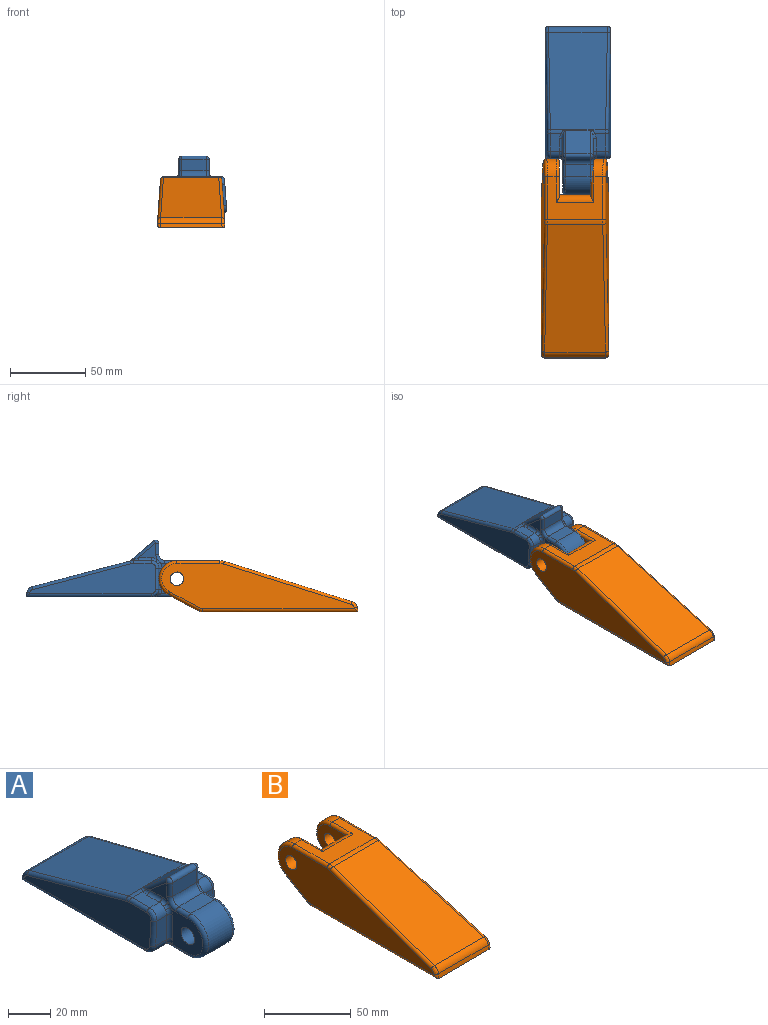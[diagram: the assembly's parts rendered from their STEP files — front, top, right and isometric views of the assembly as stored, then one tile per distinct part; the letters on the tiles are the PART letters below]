
ASSEMBLY  parts=2 mates=1
PART A: 80 faces, bbox 43.7x113x38.7 mm
  f0: plane 21.21x20.93mm, normal (1,0,0), area 295.5mm2, adj f21,f47,f48,f49,f58,f60,f61,f62
  f1: plane 21.21x20.93mm, normal (-1,0,0), area 295.5mm2, adj f21,f44,f45,f46,f54,f76,f77,f78
  f2: plane 11.71x6.91mm, normal (0,0,1), area 74.4mm2, adj f3,f10,f36,f65,f66
  f3: cylinder r=5mm len=6.51mm, axis (-1,0,0), area 50.3mm2, adj f2,f4,f35,f62,f63,f64
  f4: plane 14x7.48mm, normal (0,-1,0), area 97.9mm2, adj f3,f5,f37,f61
  f5: cylinder r=5mm len=11.69mm, axis (-1,0,0), area 68.1mm2, adj f4,f6,f39,f59,f60
  f6: plane 100x39.39mm, normal (0,0,-1), area 3541.3mm2, adj f5,f7,f14,f20,f32,f41,f44,f47
  f7: plane 39.72x2.75mm, normal (0,0.98,0.17), area 110.5mm2, adj f6,f8,f32,f34,f41,f43
  f8: cylinder r=5mm len=39.33mm, axis (-1,0,0), area 223.2mm2, adj f7,f9,f33,f42
  f9: plane 64.62x39.01mm, normal (0,0.25,0.97), area 2517.9mm2, adj f8,f10,f15,f31,f40,f68,f69,f70
  f10: cylinder r=10mm len=9.08mm, axis (-1,0,0), area 20mm2, adj f2,f9,f38,f67
  f11: plane 11.71x6.91mm, normal (0,0,1), area 74.4mm2, adj f12,f15,f27,f72,f73
  f12: cylinder r=5mm len=6.51mm, axis (-1,0,0), area 50.3mm2, adj f11,f13,f26,f74,f75,f76
  f13: plane 14x7.48mm, normal (0,-1,0), area 97.9mm2, adj f12,f14,f28,f77
  f14: cylinder r=5mm len=11.69mm, axis (-1,0,0), area 68.1mm2, adj f6,f13,f30,f78,f79
  f15: cylinder r=10mm len=9.08mm, axis (-1,0,0), area 20mm2, adj f9,f11,f29,f71
  f16: plane 16x15.61mm, normal (0,0.65,0.76), area 327.5mm2, adj f17,f51,f55,f69
  f17: cylinder r=2mm len=16mm, axis (-1,0,0), area 72.8mm2, adj f16,f18,f52,f56
  f18: plane 16x7.68mm, normal (0,-1,0), area 122.9mm2, adj f17,f50,f53,f57
  f19: plane 16x8mm, normal (0,0,1), area 128mm2, adj f20,f46,f49,f50
  f20: cylinder r=12mm len=24mm, axis (-1,0,0), area 603.2mm2, adj f6,f19,f45,f48
  f21: cylinder r=4.5mm len=20mm, axis (-1,0,0), area 565.5mm2, adj f0,f1
  f22: plane 12.34x10.89mm, normal (1,0,0), area 56.6mm2, adj f55,f57,f58,f64,f65
  f23: plane 12.34x10.89mm, normal (-1,0,0), area 56.6mm2, adj f51,f53,f54,f73,f74
  f24: plane 83.62x20mm, normal (1,0,0.07), area 1065.6mm2, adj f35,f36,f37,f38,f39,f40,f41,f42
  f25: plane 83.62x20mm, normal (-1,0,0.07), area 1065.6mm2, adj f26,f27,f28,f29,f30,f31,f32,f33
  f26: bspline ~5.87x5.87mm, area 20.4mm2, adj f12,f25,f27,f28
  f27: cylinder r=2mm len=11.71mm, axis (0,-1,0), area 35.2mm2, adj f11,f25,f26,f29
  f28: cylinder r=2mm len=14.14mm, axis (-0.07,0,-1), area 44.1mm2, adj f13,f25,f26,f30
  f29: bspline ~3.45x2.22mm, area 7.1mm2, adj f15,f25,f27,f31
  f30: bspline ~5.36x5.01mm, area 21.8mm2, adj f14,f25,f28,f32
  f31: cylinder r=2mm len=65.12mm, axis (0.02,-0.97,0.25), area 200.9mm2, adj f9,f25,f29,f33
  f32: cylinder r=2mm len=83mm, axis (0,1,0), area 269.6mm2, adj f6,f7,f25,f30,f34
  f33: bspline ~4.18x4.16mm, area 14.8mm2, adj f8,f25,f31,f34
  f34: cylinder r=2mm len=2.98mm, axis (0.07,-0.17,0.98), area 6mm2, adj f7,f25,f32,f33
  f35: bspline ~5.87x5.01mm, area 20.4mm2, adj f3,f24,f36,f37
  f36: cylinder r=2mm len=11.71mm, axis (0,1,0), area 35.2mm2, adj f2,f24,f35,f38
  f37: cylinder r=2mm len=14.14mm, axis (-0.07,0,1), area 44.1mm2, adj f4,f24,f35,f39
  f38: bspline ~3.01x2.22mm, area 7.1mm2, adj f10,f24,f36,f40
  f39: bspline ~5.36x5.23mm, area 21.8mm2, adj f5,f24,f37,f41
  f40: cylinder r=2mm len=65.12mm, axis (0.02,0.97,-0.25), area 200.9mm2, adj f9,f24,f38,f42
  f41: cylinder r=2mm len=83mm, axis (0,-1,0), area 269.6mm2, adj f6,f7,f24,f39,f43
  f42: bspline ~4.18x4.16mm, area 14.8mm2, adj f8,f24,f40,f43
  f43: cylinder r=2mm len=2.98mm, axis (0.07,0.17,-0.98), area 6mm2, adj f7,f24,f41,f42
  f44: cylinder r=2mm len=17mm, axis (0,1,0), area 42mm2, adj f1,f6,f45,f79
  f45: torus R=10mm, axis (1,0,0), area 111.3mm2, adj f1,f20,f44,f46
  f46: cylinder r=2mm len=8mm, axis (0,-1,0), area 25.1mm2, adj f1,f19,f45,f54
  f47: cylinder r=2mm len=17mm, axis (0,-1,0), area 42mm2, adj f0,f6,f48,f59
  f48: torus R=10mm, axis (1,0,0), area 111.3mm2, adj f0,f20,f47,f49
  f49: cylinder r=2mm len=8mm, axis (0,1,0), area 25.1mm2, adj f0,f19,f48,f58
  f50: cylinder r=4mm len=16mm, axis (1,0,0), area 100.5mm2, adj f18,f19,f54,f58
  f51: cylinder r=2mm len=16.9mm, axis (0,-0.76,0.65), area 57mm2, adj f16,f23,f52,f70,f71,f72
  f52: sphere r=2mm, area 9.1mm2, adj f17,f51,f53
  f53: cylinder r=2mm len=7.68mm, axis (0,0,-1), area 24.1mm2, adj f18,f23,f52,f54
  f54: torus R=6mm, axis (1,0,0), area 23.1mm2, adj f1,f23,f46,f50,f53,f75
  f55: cylinder r=2mm len=16.9mm, axis (0,0.76,-0.65), area 57mm2, adj f16,f22,f56,f66,f67,f68
  f56: sphere r=2mm, area 9.1mm2, adj f17,f55,f57
  f57: cylinder r=2mm len=7.68mm, axis (0,0,1), area 24.1mm2, adj f18,f22,f56,f58
  f58: torus R=6mm, axis (1,0,0), area 23.1mm2, adj f0,f22,f49,f50,f57,f63
  f59: bspline ~6.64x4mm, area 10.5mm2, adj f5,f47,f60
  f60: torus R=7mm, axis (1,0,0), area 8mm2, adj f0,f5,f59,f61
  f61: cylinder r=2mm len=14mm, axis (0,0,-1), area 44mm2, adj f0,f4,f60,f62
  f62: torus R=7mm, axis (1,0,0), area 10.7mm2, adj f0,f3,f61,f63
  f63: bspline ~4.52x4.52mm, area 6.6mm2, adj f3,f58,f62,f64
  f64: torus R=7mm, axis (1,0,0), area 10.7mm2, adj f3,f22,f63,f65
  f65: cylinder r=2mm len=8.41mm, axis (0,-1,0), area 26.4mm2, adj f2,f22,f64,f66
  f66: bspline ~5.05x2.47mm, area 8mm2, adj f2,f55,f65,f67
  f67: bspline ~3.64x3.05mm, area 5.1mm2, adj f10,f55,f66,f68
  f68: bspline ~1.24x1.16mm, area 1mm2, adj f9,f55,f67,f69
  f69: cylinder r=2mm len=16mm, axis (-1,0,0), area 14.3mm2, adj f9,f16,f68,f70
  f70: bspline ~1.24x1.16mm, area 1mm2, adj f9,f51,f69,f71
  f71: bspline ~3.64x3.05mm, area 5.1mm2, adj f15,f51,f70,f72
  f72: bspline ~3.3x2.31mm, area 8mm2, adj f11,f51,f71,f73
  f73: cylinder r=2mm len=8.41mm, axis (0,1,0), area 26.4mm2, adj f11,f23,f72,f74
  f74: torus R=7mm, axis (1,0,0), area 10.7mm2, adj f12,f23,f73,f75
  f75: bspline ~4.52x4.52mm, area 6.6mm2, adj f12,f54,f74,f76
  f76: torus R=7mm, axis (1,0,0), area 10.7mm2, adj f1,f12,f75,f77
  f77: cylinder r=2mm len=14mm, axis (0,0,1), area 44mm2, adj f1,f13,f76,f78
  f78: torus R=7mm, axis (1,0,0), area 8mm2, adj f1,f14,f77,f79
  f79: bspline ~6.64x4mm, area 10.5mm2, adj f14,f44,f78
PART B: 43 faces, bbox 45.1x133x35.2 mm
  f0: plane 36.59x28.46mm, normal (0,0,1), area 616.3mm2, adj f3,f4,f11,f15,f20,f29,f37,f40
  f1: cylinder r=5mm len=40.79mm, axis (-1,0,0), area 220.4mm2, adj f2,f8,f10,f13,f14,f16,f23,f32
  f2: plane 20.29x10.82mm, normal (0,0.47,-0.88), area 172.3mm2, adj f1,f3,f30,f39
  f3: cylinder r=12mm len=22.59mm, axis (-1,0,0), area 202.7mm2, adj f0,f2,f28,f38
  f4: cylinder r=10mm len=36.64mm, axis (-1,0,0), area 112mm2, adj f0,f5,f22,f31
  f5: plane 84.6x40.38mm, normal (0,-0.3,0.95), area 3416.5mm2, adj f4,f6,f24,f33
  f6: cylinder r=5mm len=40.71mm, axis (-1,0,0), area 221mm2, adj f5,f7,f26,f35
  f7: plane 41.12x2.92mm, normal (0,-0.98,0.17), area 121.4mm2, adj f6,f8,f25,f27,f34,f36
  f8: plane 103x40.79mm, normal (0,0,-1), area 4201.1mm2, adj f1,f7,f25,f34
  f9: cylinder r=4.5mm len=10.82mm, axis (-1,0,0), area 296.9mm2, adj f14,f17
  f10: plane 20.29x10.82mm, normal (0,0.47,-0.88), area 172.3mm2, adj f1,f11,f21,f42
  f11: cylinder r=12mm len=22.59mm, axis (-1,0,0), area 202.7mm2, adj f0,f10,f19,f41
  f12: cylinder r=4.5mm len=10.82mm, axis (-1,0,0), area 296.9mm2, adj f13,f18
  f13: plane 27.76x23mm, normal (1,0,0), area 391mm2, adj f1,f12,f15,f16,f40,f41,f42
  f14: plane 27.76x23mm, normal (-1,0,0), area 391mm2, adj f1,f9,f15,f16,f37,f38,f39
  f15: cylinder r=5mm len=25mm, axis (1,0,0), area 172mm2, adj f0,f13,f14,f16,f37,f40
  f16: plane 24x21mm, normal (0,1,0), area 504mm2, adj f1,f13,f14,f15
  f17: plane 127.62x30mm, normal (1,0,0.07), area 2337.7mm2, adj f9,f28,f29,f30,f31,f32,f33,f34
  f18: plane 127.62x30mm, normal (-1,0,0.07), area 2337.7mm2, adj f12,f19,f20,f21,f22,f23,f24,f25
  f19: bspline ~22.59x12mm, area 93.2mm2, adj f11,f18,f20,f21
  f20: cylinder r=2mm len=28.46mm, axis (0,-1,0), area 85.4mm2, adj f0,f18,f19,f22
  f21: cylinder r=2mm len=21.24mm, axis (0.03,0.88,0.47), area 75.1mm2, adj f10,f18,f19,f23
  f22: bspline ~5.97x2.6mm, area 8.5mm2, adj f4,f18,f20,f24
  f23: bspline ~2.76x2.61mm, area 6.9mm2, adj f1,f18,f21,f25
  f24: cylinder r=2mm len=85.2mm, axis (-0.02,-0.95,-0.3), area 267mm2, adj f5,f18,f22,f26
  f25: cylinder r=2mm len=103mm, axis (0,1,0), area 335.2mm2, adj f7,f8,f18,f23,f27
  f26: bspline ~4.49x4.34mm, area 14.2mm2, adj f6,f18,f24,f27
  f27: cylinder r=2mm len=3.15mm, axis (-0.07,-0.17,-0.98), area 6.5mm2, adj f7,f18,f25,f26
  f28: bspline ~22.59x12mm, area 93.2mm2, adj f3,f17,f29,f30
  f29: cylinder r=2mm len=28.46mm, axis (0,1,0), area 85.4mm2, adj f0,f17,f28,f31
  f30: cylinder r=2mm len=21.24mm, axis (0.03,-0.88,-0.47), area 75.1mm2, adj f2,f17,f28,f32
  f31: bspline ~4.23x2.6mm, area 8.5mm2, adj f4,f17,f29,f33
  f32: bspline ~3.65x2.61mm, area 6.9mm2, adj f1,f17,f30,f34
  f33: cylinder r=2mm len=85.2mm, axis (-0.02,0.95,0.3), area 267mm2, adj f5,f17,f31,f35
  f34: cylinder r=2mm len=103mm, axis (0,-1,0), area 335.2mm2, adj f7,f8,f17,f32,f36
  f35: bspline ~4.49x4.34mm, area 14.2mm2, adj f6,f17,f33,f36
  f36: cylinder r=2mm len=3.15mm, axis (-0.07,0.17,0.98), area 6.5mm2, adj f7,f17,f34,f35
  f37: cylinder r=2mm len=17mm, axis (0,1,0), area 46.4mm2, adj f0,f14,f15,f38
  f38: torus R=10mm, axis (1,0,0), area 93.9mm2, adj f3,f14,f37,f39
  f39: cylinder r=2mm len=21.24mm, axis (0,0.88,0.47), area 65.3mm2, adj f1,f2,f14,f38
  f40: cylinder r=2mm len=17mm, axis (0,-1,0), area 46.4mm2, adj f0,f13,f15,f41
  f41: torus R=10mm, axis (1,0,0), area 93.9mm2, adj f11,f13,f40,f42
  f42: cylinder r=2mm len=21.24mm, axis (0,-0.88,-0.47), area 65.3mm2, adj f1,f10,f13,f41
PLACE A t=(-23.24,28.94,-23.99)mm fixed
PLACE B t=(-25.11,28.94,-23.99)mm
MATE revolute A.f21 <-> B.f9  axis (-1,0,0) through (-23.24,28.94,-11.99)mm
